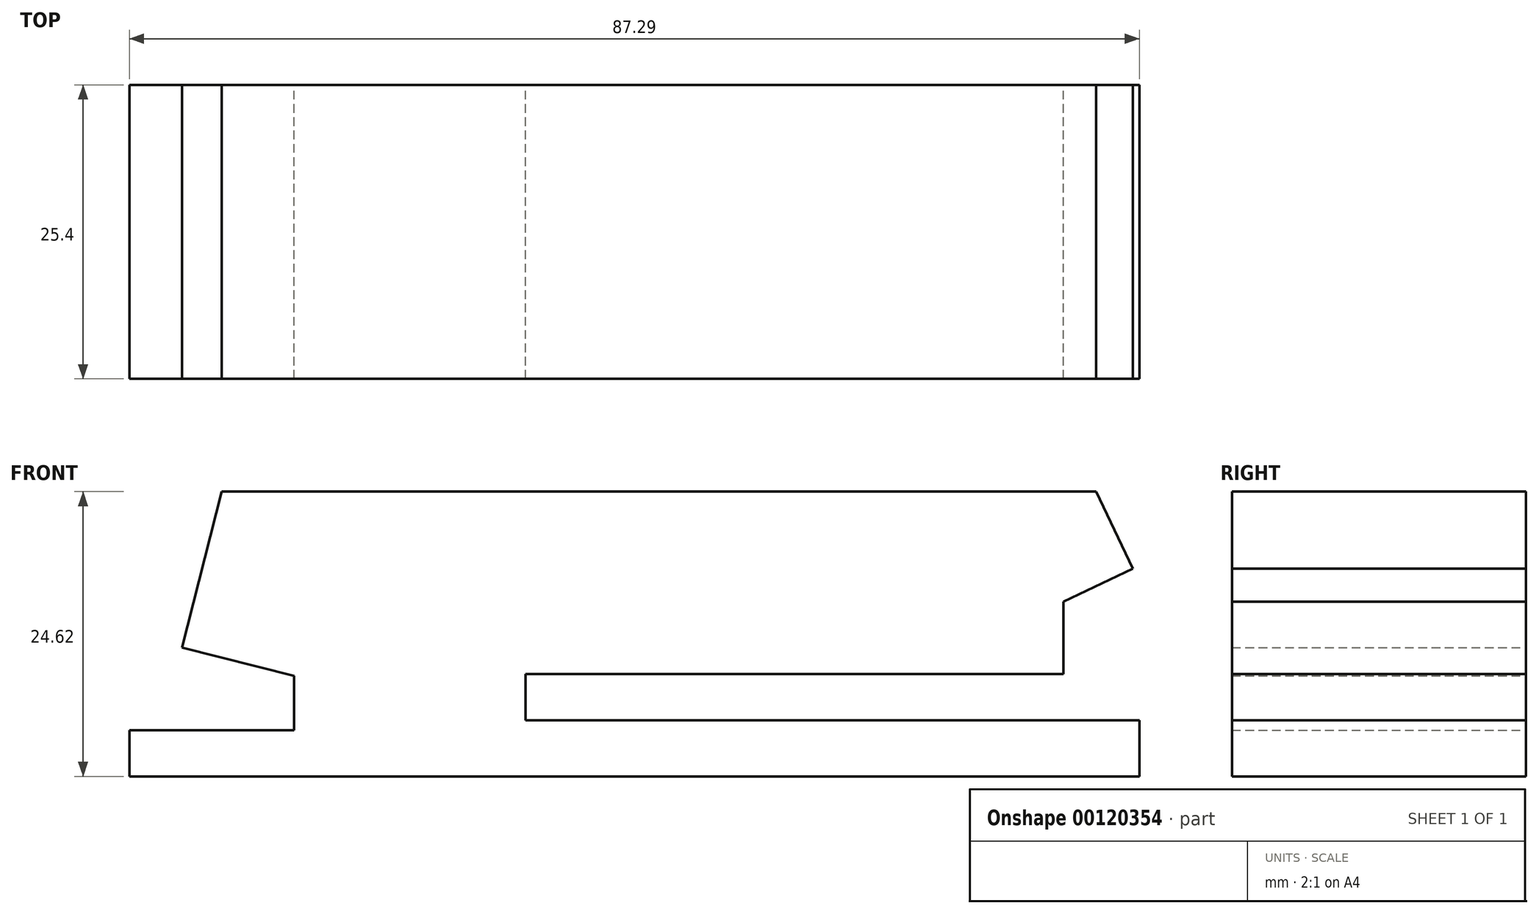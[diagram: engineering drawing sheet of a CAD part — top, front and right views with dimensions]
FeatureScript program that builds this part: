
annotation { "Feature Type Name" : "Feature", "Feature Type Description" : "" }
export const myFeature = defineFeature(function(context is Context, id is Id, definition is map)
    precondition{}
    {
        {
            var Q0;
            Q0=qCreatedBy(makeId("Front.planeOp"),FACE);
            var sketch = newSketch(context, id + "F0", { "sketchPlane" : qUnion([Q0])});
            skLineSegment(sketch, "E0", {"start": v(-53.63, 5.85) * mm, "end": v(33.66, 5.85) * mm});
            skLineSegment(sketch, "E1", {"start": v(33.66, 5.85) * mm, "end": v(33.66, 10.7) * mm});
            skLineSegment(sketch, "E2", {"start": v(33.66, 10.7) * mm, "end": v(-19.4, 10.7) * mm});
            skLineSegment(sketch, "E3", {"start": v(-19.4, 10.7) * mm, "end": v(-19.4, 14.69) * mm});
            skLineSegment(sketch, "E4", {"start": v(-19.4, 14.69) * mm, "end": v(27.1, 14.69) * mm});
            skLineSegment(sketch, "E5", {"start": v(27.1, 14.69) * mm, "end": v(27.1, 20.97) * mm});
            skLineSegment(sketch, "E6", {"start": v(27.1, 20.97) * mm, "end": v(33.09, 23.82) * mm});
            skLineSegment(sketch, "E7", {"start": v(33.09, 23.82) * mm, "end": v(29.92, 30.47) * mm});
            skLineSegment(sketch, "E8", {"start": v(29.92, 30.47) * mm, "end": v(-45.64, 30.47) * mm});
            skLineSegment(sketch, "E9", {"start": v(-45.64, 30.47) * mm, "end": v(-49.06, 16.97) * mm});
            skLineSegment(sketch, "E10", {"start": v(-49.06, 16.97) * mm, "end": v(-39.4, 14.52) * mm});
            skLineSegment(sketch, "E11", {"start": v(-39.4, 14.52) * mm, "end": v(-39.4, 9.84) * mm});
            skLineSegment(sketch, "E12", {"start": v(-39.4, 9.84) * mm, "end": v(-53.63, 9.84) * mm});
            skLineSegment(sketch, "E13", {"start": v(-53.63, 9.84) * mm, "end": v(-53.63, 5.85) * mm});
            skSolve(sketch);
        }
        {
            var Q0;
            Q0 = qSketchRegion(id + "F0", true);
            extrude(context, id + "F1", {"entities" : qUnion([Q0]), "depth" : 25.4 * mm});
        }
    });
